# Revit family: Toilet-Floor_Outlet-Whitehall-BestCare-WH2142-ADA-W-EGE10_Series
name_source: partatom
category: Plumbing Fixtures
revit_build: Autodesk Revit 2018 (Build: 20170223_1515(x64)
units: mm (PartAtom-declared; Revit-internal decimal feet)

## family parameters
Cut with Voids When Loaded = No
Host = Face
OmniClass Number = 23.45.05.21.11.11
OmniClass Title = Water Operated Water Closets
Part Type = Normal
Room Calculation Point = No
Round Connector Dimension = Use Diameter
Shared = Yes

## types (2) — shared parameters
-HET 1.28 Hydraulic GPF = No
-ULF 1.6 Hydraulic GPF = No
ADA Compliant = Yes
Assembly Code = D2010110
Body Material = Stainless Steel-Whitehall-Powder Coated White
Bowl Shape = Elongated
CW Connection = Yes
CWFU = 5
Connection Type = 1-1/2" Female NPT Inlet Connection
Default Elevation = 0"
Description = Whitehall Ligature Resistant Cistern Tank Toilet
Flush Rate = 1.28 gpf
Flush Valve Height = 36"
Flush Valve Height Constraint = 36"
HW Connection = No
Height = 18 3/8"
Inlet Connection Diameter = 1 1/2"
Inlet Connection Height = 16"
Inlet Connection Radius = 3/4"
Installation Type = Floor Mounted
Length = 29 1/4"
Manufacturer = Whitehall Mfg
Material = Stainless Steel-Whitehall-Powder Coated White
Minimum Flowing Pressure = 25.00 psi
Price = Prices may vary. Please consult Manufacturer Representative for most up-to-date price list.
Product Documentation Link = https://www.whitehallmfg.com
Product Page URL = https://www.whitehallmfg.com
Revised Date = 04/21/2022
Seat Cover Material = Stainless Steel-Whitehall-WH-LRSC_GRAY
Seat Cover WH-LRSC-BLACK Ligature Resistant Seat Cover, Black (Shipped Loose) = No
Seat Cover WH-LRSC-BLUE Ligature Resistant Seat Cover, Dignity Blue (Shipped Loose) = No
Seat Cover WH-LRSC-WHITE Ligature Resistant Seat Cover, White (Shipped Loose) = No
URL = http://www.whitehallmfg.com
Vent Connection = No
WFU = 5
Waste Connection = Yes
Waste Connection Diameter = 2 3/8"
Waste Connection Radius = 1 3/16"
Width = 14 3/4"
zero-valued in all types: HWFU

## per-type parameters (varying)
| type | Waste Connection Distance From Wall |
| WH2142-ADA-W-3-EGE10_10 | 10" |
| WH2142-ADA-W-3-EGE10_12 | 12" |

note: column(s) folded — value = type name in every type: Model

## geometry (parser evidence)
native form markers: Sweep x3
no freeform markers — native parametric forms only
